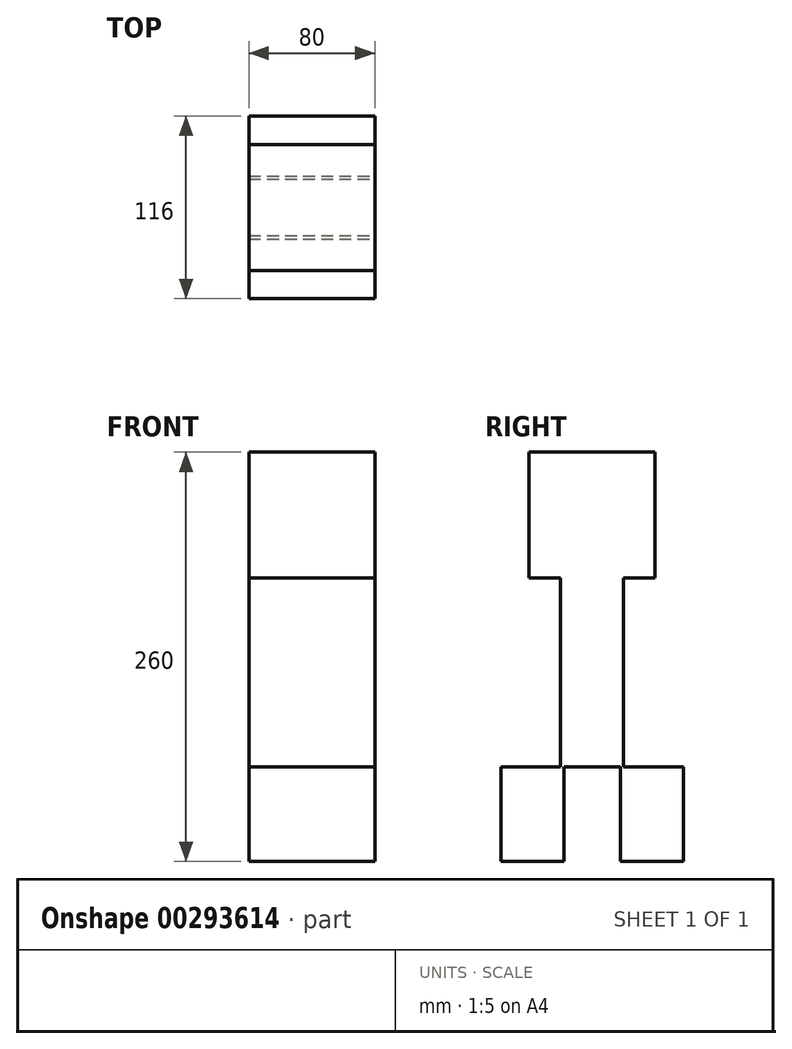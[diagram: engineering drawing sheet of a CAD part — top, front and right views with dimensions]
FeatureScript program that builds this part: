
annotation { "Feature Type Name" : "Feature", "Feature Type Description" : "" }
export const myFeature = defineFeature(function(context is Context, id is Id, definition is map)
    precondition{}
    {
        {
            var Q0;
            Q0=qCreatedBy(makeId("Top.planeOp"),FACE);
            var sketch = newSketch(context, id + "F0", { "sketchPlane" : qUnion([Q0])});
            skLineSegment(sketch, "E0.bottom", {"start": v(-57.93, 50.02) * mm, "end": v(22.07, 50.02) * mm});
            skLineSegment(sketch, "E0.top", {"start": v(-57.93, -29.98) * mm, "end": v(22.07, -29.98) * mm});
            skLineSegment(sketch, "E0.left", {"start": v(-57.93, 50.02) * mm, "end": v(-57.93, -29.98) * mm});
            skLineSegment(sketch, "E0.right", {"start": v(22.07, 50.02) * mm, "end": v(22.07, -29.98) * mm});
            skSolve(sketch);
        }
        {
            var Q0;
            Q0 = qSketchRegion(id + "F0", true);
            extrude(context, id + "F1", {"entities" : qUnion([Q0]), "depth" : 80 * mm});
        }
        {
            var Q0;
            Q0=makeQuery(id+"F1.opExtrude","CAP_FACE",FACE,{"disambiguationData":[OSD([sQuery(id+"F0.wireOp",EDGE,"E0.bottom"),sQuery(id+"F0.wireOp",EDGE,"E0.top"),sQuery(id+"F0.wireOp",EDGE,"E0.left"),sQuery(id+"F0.wireOp",EDGE,"E0.right")])],"isStart":true});
            var sketch = newSketch(context, id + "F2", { "sketchPlane" : qUnion([Q0])});
            skLineSegment(sketch, "E1.bottom", {"start": v(-57.93, 9.98) * mm, "end": v(22.07, 9.98) * mm});
            skLineSegment(sketch, "E1.top", {"start": v(-57.93, -30.02) * mm, "end": v(22.07, -30.02) * mm});
            skLineSegment(sketch, "E1.left", {"start": v(-57.93, 9.98) * mm, "end": v(-57.93, -30.02) * mm});
            skLineSegment(sketch, "E1.right", {"start": v(22.07, 9.98) * mm, "end": v(22.07, -30.02) * mm});
            skSolve(sketch);
        }
        {
            var Q0;
            Q0 = qSketchRegion(id + "F2", true);
            extrude(context, id + "F3", {"entities" : qUnion([Q0]), "operationType" : NewBodyOperationType.ADD, "depth" : 120 * mm});
        }
        {
            var Q0;
            Q0=makeQuery(id+"F3.opExtrude","CAP_FACE",FACE,{"disambiguationData":[OSD([sQuery(id+"F2.wireOp",EDGE,"E1.bottom"),sQuery(id+"F2.wireOp",EDGE,"E1.top"),sQuery(id+"F2.wireOp",EDGE,"E1.left"),sQuery(id+"F2.wireOp",EDGE,"E1.right")])],"isStart":false});
            var sketch = newSketch(context, id + "F4", { "sketchPlane" : qUnion([Q0])});
            skLineSegment(sketch, "E2.bottom", {"start": v(-57.93, 7.98) * mm, "end": v(22.07, 7.98) * mm});
            skLineSegment(sketch, "E2.top", {"start": v(-57.93, 47.98) * mm, "end": v(22.07, 47.98) * mm});
            skLineSegment(sketch, "E2.left", {"start": v(-57.93, 7.98) * mm, "end": v(-57.93, 47.98) * mm});
            skLineSegment(sketch, "E2.right", {"start": v(22.07, 7.98) * mm, "end": v(22.07, 47.98) * mm});
            skLineSegment(sketch, "E3.bottom", {"start": v(-57.93, -28.02) * mm, "end": v(22.07, -28.02) * mm});
            skLineSegment(sketch, "E3.top", {"start": v(-57.93, -68.02) * mm, "end": v(22.07, -68.02) * mm});
            skLineSegment(sketch, "E3.left", {"start": v(-57.93, -28.02) * mm, "end": v(-57.93, -68.02) * mm});
            skLineSegment(sketch, "E3.right", {"start": v(22.07, -28.02) * mm, "end": v(22.07, -68.02) * mm});
            skSolve(sketch);
        }
        {
            var Q0;
            Q0 = qSketchRegion(id + "F4", true);
            extrude(context, id + "F5", {"entities" : qUnion([Q0]), "operationType" : NewBodyOperationType.ADD, "depth" : 60 * mm});
        }
    });
